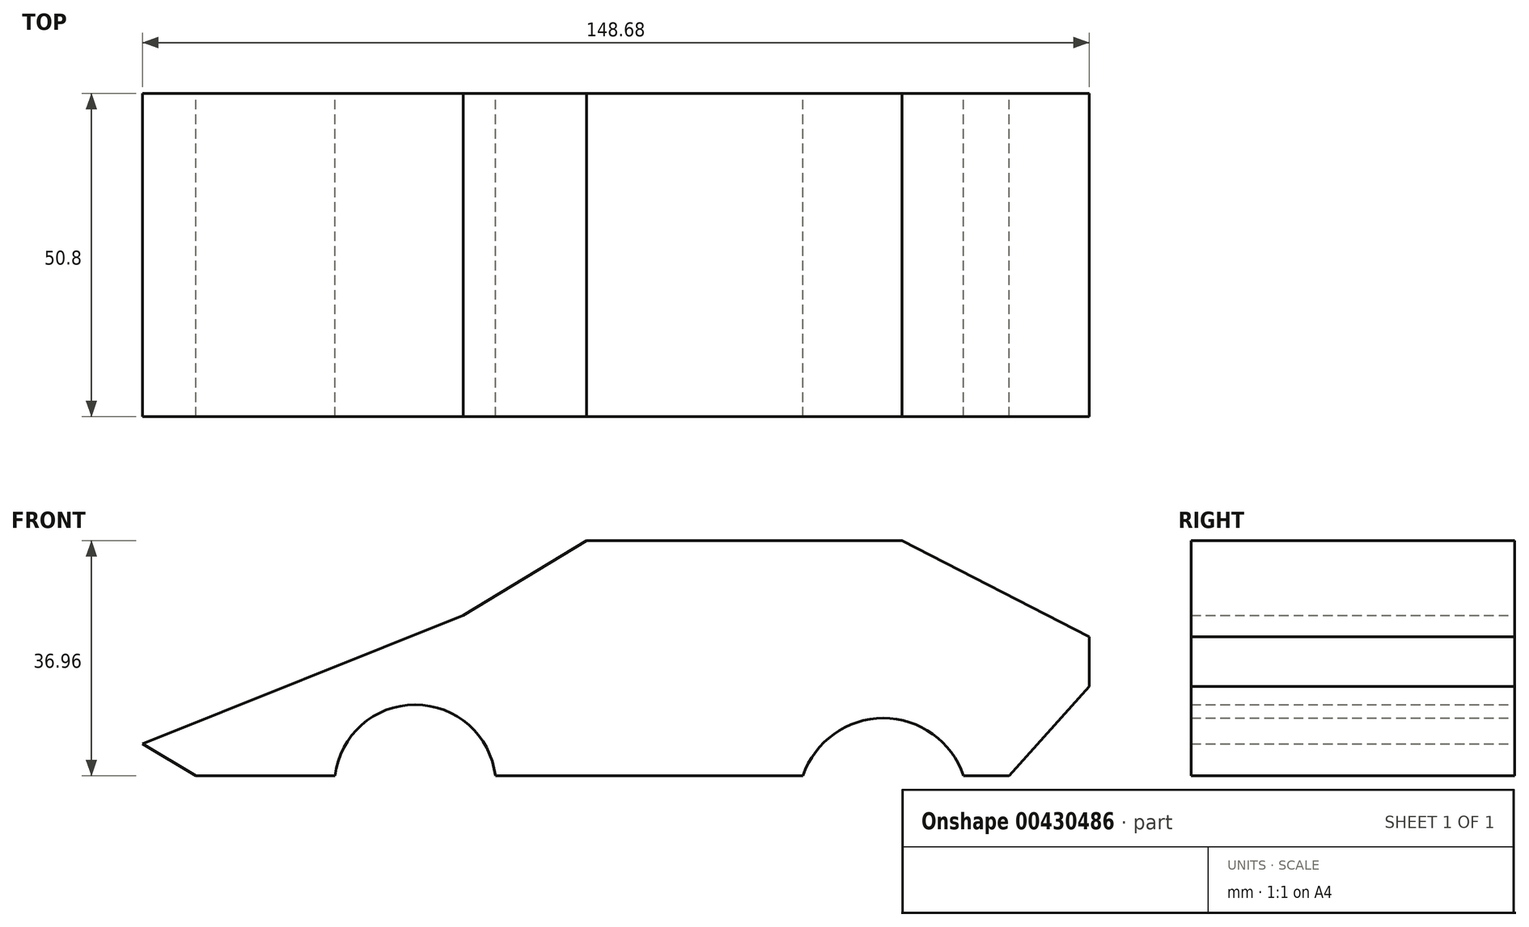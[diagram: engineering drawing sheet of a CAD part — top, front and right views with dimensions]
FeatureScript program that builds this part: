
annotation { "Feature Type Name" : "Feature", "Feature Type Description" : "" }
export const myFeature = defineFeature(function(context is Context, id is Id, definition is map)
    precondition{}
    {
        {
            var Q0;
            Q0=qCreatedBy(makeId("Front.planeOp"),FACE);
            var sketch = newSketch(context, id + "F0", { "sketchPlane" : qUnion([Q0])});
            skLineSegment(sketch, "E0", {"start": v(-120.54, -14.07) * mm, "end": v(-98.7, -14.07) * mm});
            skArc(sketch, "E1", {"start": v(-73.5, -14.07) * mm, "mid": v(-86.1, -2.9) * mm, "end": v(-98.7, -14.07) * mm});
            skLineSegment(sketch, "E2", {"start": v(-120.54, -14.07) * mm, "end": v(-128.94, -9.03) * mm});
            skLineSegment(sketch, "E3", {"start": v(-128.94, -9.03) * mm, "end": v(-78.54, 11.13) * mm});
            skLineSegment(sketch, "E4", {"start": v(-78.54, 11.13) * mm, "end": v(-59.22, 22.89) * mm});
            skLineSegment(sketch, "E5", {"start": v(-59.22, 22.89) * mm, "end": v(-9.66, 22.89) * mm});
            skLineSegment(sketch, "E6", {"start": v(-9.66, 22.89) * mm, "end": v(19.74, 7.77) * mm});
            skLineSegment(sketch, "E7", {"start": v(19.74, 7.77) * mm, "end": v(19.74, 0) * mm});
            skLineSegment(sketch, "E8", {"start": v(19.74, 0) * mm, "end": v(7.14, -14.07) * mm});
            skLineSegment(sketch, "E9", {"start": v(7.14, -14.07) * mm, "end": v(0, -14.07) * mm});
            skArc(sketch, "E10", {"start": v(0, -14.07) * mm, "mid": v(-12.6, -5.01) * mm, "end": v(-25.2, -14.07) * mm});
            skLineSegment(sketch, "E11", {"start": v(-73.5, -14.07) * mm, "end": v(-25.2, -14.07) * mm});
            skLineSegment(sketch, "E12", {"start": v(-78.54, 11.13) * mm, "end": v(13.2, 11.13) * mm});
            skLineSegment(sketch, "E13", {"start": v(-78.54, 11.13) * mm, "end": v(-78.54, -5.4) * mm});
            skPoint(sketch, "E14", {"position": v(-34.44, 11.13) * mm});
            skPoint(sketch, "E14.positionSnap0", {"position": v(-34.44, 22.89) * mm});
            skLineSegment(sketch, "E15", {"start": v(-34.44, 11.13) * mm, "end": v(-34.44, -14.07) * mm});
            skLineSegment(sketch, "E16", {"start": v(-6.56, -6.46) * mm, "end": v(-6.56, 11.13) * mm});
            skLineSegment(sketch, "E17", {"start": v(-41.07, 5.25) * mm, "end": v(-48.63, 5.25) * mm});
            skLineSegment(sketch, "E18", {"start": v(-11.67, 6.93) * mm, "end": v(-18.39, 6.93) * mm});
            skSolve(sketch);
        }
        {
            var Q0;
            Q0 = qSketchRegion(id + "F0", true);
            extrude(context, id + "F1", {"entities" : qUnion([Q0]), "depth" : 50.8 * mm});
        }
    });
